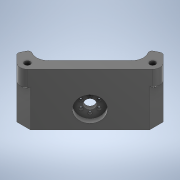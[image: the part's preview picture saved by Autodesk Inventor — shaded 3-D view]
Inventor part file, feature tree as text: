
AUTODESK INVENTOR PART (.ipt)
format: ipt  version: 2020 (Build 240168000, 168)  size: 335,360 bytes
history: native  units: mm
features: sketch x9, extrude x8, chamfer x3, projected_geometry x3, other x1, fillet x1
ambient origin geometry x8: Origin, YZ Plane, XZ Plane, XY Plane, X Axis, Y Axis, Z Axis, Center Point
bodies: Body1 (feature_tree)
feature tree (25):
  other  "Твердое тело1"
  extrude  "Выдавливание1"  Depth=35.0mm TaperAngle=0.0deg
  sketch  "Эскиз2"
  extrude  "Выдавливание4"  Depth=20.6mm
  extrude  "Выдавливание5"  Depth=15.0mm
  sketch  "Эскиз5"
  extrude  "Выдавливание8"  Depth=2.5mm
  extrude  "Выдавливание9"  Depth=60.0mm TaperAngle=360.0deg
  chamfer  "Фаска2"  Distance=11.0mm
  sketch  "Эскиз6"
  extrude  "Выдавливание10"  Depth=3.8mm
  fillet  "Сопряжение1"  Radius=3.8mm
  extrude  "Выдавливание11"  Depth=40.5mm TaperAngle=0.0deg
  extrude  "Выдавливание12"  Depth=4.0mm
  chamfer  "Фаска3"  Distance=4.0mm
  chamfer  "Фаска4"  Distance=3.5mm
  sketch  "Эскиз1"
  projected_geometry  "Спроецированная петля1"
  sketch  "Эскиз3"
  sketch  "Эскиз4"
  projected_geometry  "Спроецированная петля2"
  sketch  "Эскиз7"
  sketch  "Эскиз8"
  projected_geometry  "Спроецированная петля3"
  sketch  "Эскиз9"
